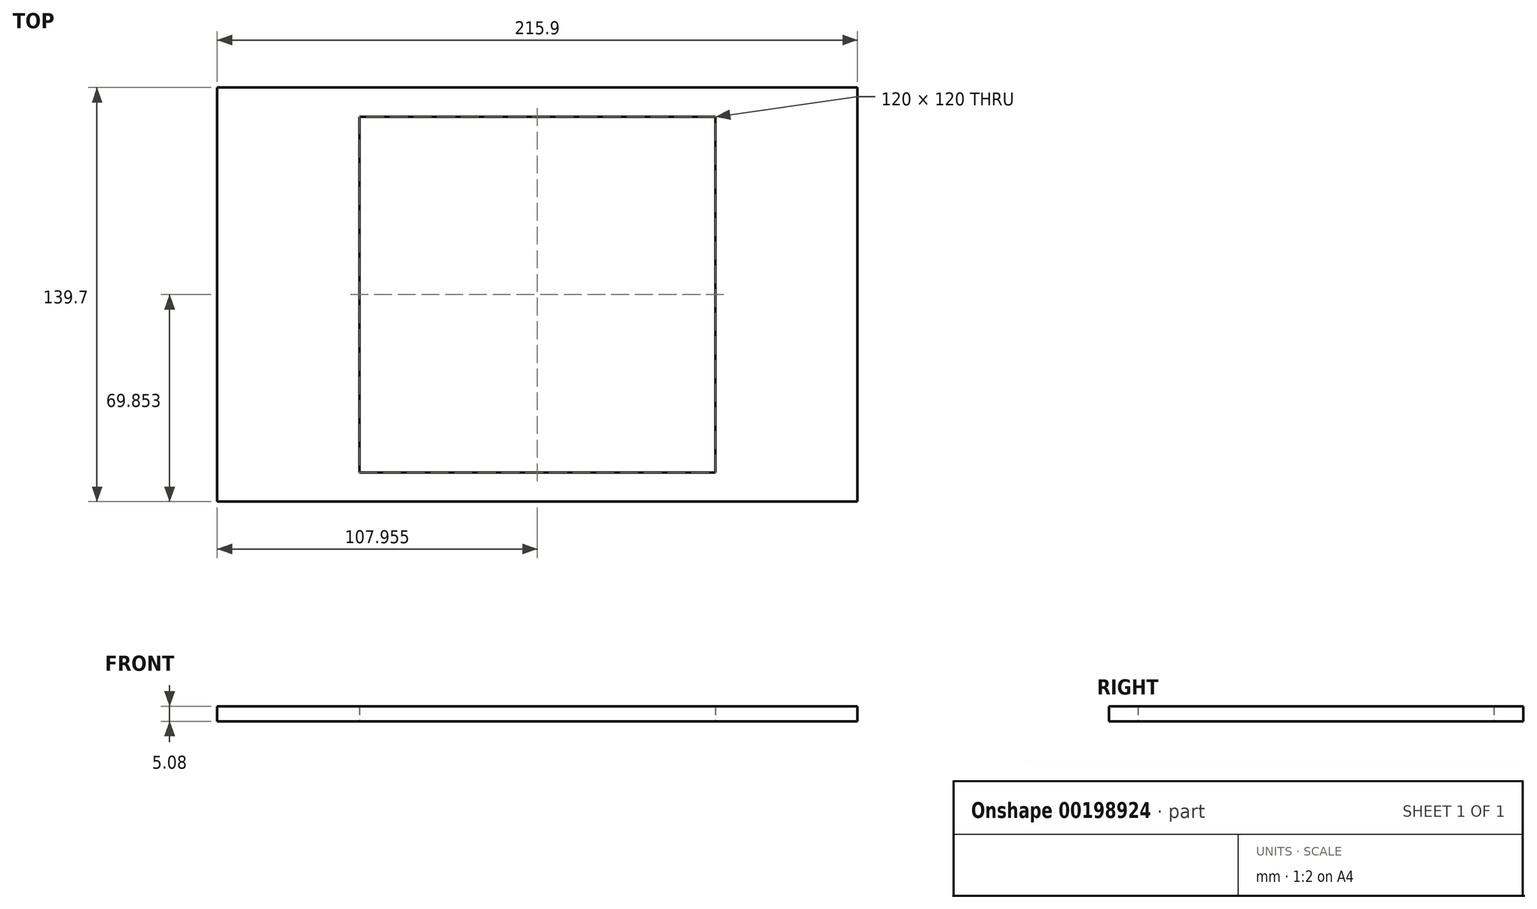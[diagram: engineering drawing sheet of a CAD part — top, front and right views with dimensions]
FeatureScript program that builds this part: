
annotation { "Feature Type Name" : "Feature", "Feature Type Description" : "" }
export const myFeature = defineFeature(function(context is Context, id is Id, definition is map)
    precondition{}
    {
        {
            var Q0;
            Q0=qCreatedBy(makeId("Top.planeOp"),FACE);
            var sketch = newSketch(context, id + "F0", { "sketchPlane" : qUnion([Q0])});
            skLineSegment(sketch, "E0.bottom", {"start": v(56.47, -44.36) * mm, "end": v(-159.43, -44.36) * mm});
            skLineSegment(sketch, "E0.top", {"start": v(56.47, 95.34) * mm, "end": v(-159.43, 95.34) * mm});
            skLineSegment(sketch, "E0.left", {"start": v(56.47, -44.36) * mm, "end": v(56.47, 95.34) * mm});
            skLineSegment(sketch, "E0.right", {"start": v(-159.43, -44.36) * mm, "end": v(-159.43, 95.34) * mm});
            skPoint(sketch, "E1", {"position": v(-51.48, 95.34) * mm});
            skPoint(sketch, "E2", {"position": v(56.47, 25.5) * mm});
            skLineSegment(sketch, "E3", {"start": v(-111.48, 25.5) * mm, "end": v(8.52, 25.5) * mm});
            skPoint(sketch, "E4", {"position": v(-51.48, 25.5) * mm});
            skLineSegment(sketch, "E5", {"start": v(-51.48, -34.5) * mm, "end": v(-51.48, 85.5) * mm});
            skLineSegment(sketch, "E6", {"start": v(56.47, 25.5) * mm, "end": v(-159.43, 25.5) * mm, "construction": true});
            skLineSegment(sketch, "E7", {"start": v(-111.48, 85.5) * mm, "end": v(-111.48, -34.5) * mm});
            skLineSegment(sketch, "E8", {"start": v(-111.48, 85.5) * mm, "end": v(8.52, 85.5) * mm});
            skLineSegment(sketch, "E9", {"start": v(8.52, 85.5) * mm, "end": v(8.52, -34.5) * mm});
            skLineSegment(sketch, "E10", {"start": v(8.52, -34.5) * mm, "end": v(-111.48, -34.5) * mm});
            skSolve(sketch);
        }
        {
            var Q0;
            Q0=makeQuery(id+"F0.imprint","IMPRINT",FACE,{"disambiguationData":[TD([[makeQuery(id+"F0.imprint","IMPRINT",EDGE,{"derivedFrom":sQuery(id+"F0.wireOp",EDGE,"E0.bottom")}),-1.0]])]});
            extrude(context, id + "F1", {"entities" : qUnion([Q0]), "depth" : 5.08 * mm});
        }
    });
